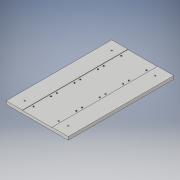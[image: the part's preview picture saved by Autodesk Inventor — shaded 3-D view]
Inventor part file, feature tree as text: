
AUTODESK INVENTOR PART (.ipt)
format: ipt  version: 2019.4 (Build 234330000, 330)  size: 196,096 bytes
history: native  units: in
note: dims shown in document units (in); Inventor stores cm internally (conversion verified against a paired STEP export)
features: projected_geometry x13, sketch x5, extrude x3, hole x2
ambient origin geometry x8: Origin, YZ Plane, XZ Plane, XY Plane, X Axis, Y Axis, Z Axis, Center Point
bodies: Solid1 (feature_tree)
feature tree (23):
  extrude  "Extrusion1"  Depth=8.5in
  hole  "Hole2"  [1 undecoded]
  extrude  "Extrusion4"  Depth=0.7874in
  extrude  "Extrusion5"  Depth=2.3819in
  hole  "Hole3"  [1 undecoded]
  sketch  "Sketch1"  dims[d0=5.0in d1=8.5in]
  sketch  "Sketch5"  dims[d2=0.25in d3=0.0in d36=0.75in]
  sketch  "Sketch6"  dims[d37=0.75in d38=0.7874in d40=7.0in d41=0.7874in d43=3.5in]
  sketch  "Sketch8"  dims[d46=0.097in d47=0.25in d48=0.385in d49=0.25in d50=0.5635in d51=0.1875in d52=0.8108in d53=2.3819in]
  sketch  "Sketch9"  dims[d54=0.025in d55=0.0in d56=0.0945in d57=0.713in d58=1.486in d59=1.421in d60=2.028in d61=1.5748in d63=1.884in d64=0.3937in d66=1.0in d68=0.025in d69=0.0in d70=0.062in d71=0.157in d72=0.375in d73=0.25in d74=0.5635in d75=0.248in d76=0.8108in]
  projected_geometry  "Projected Loop1"
  projected_geometry  "Projected Loop2"
  projected_geometry  "Projected Loop3"
  projected_geometry  "Projected Loop4"
  projected_geometry  "Projected Loop5"
  projected_geometry  "Projected Loop6"
  projected_geometry  "Projected Loop7"
  projected_geometry  "Projected Loop8"
  projected_geometry  "Projected Loop9"
  projected_geometry  "Projected Loop10"
  projected_geometry  "Projected Loop11"
  projected_geometry  "Projected Loop12"
  projected_geometry  "Projected Loop13"
note: 2 required parameter values undecoded (feature->parameter linkage not recoverable at this tier; creation-order binding heuristic only, values carry confidence <= 0.55)
